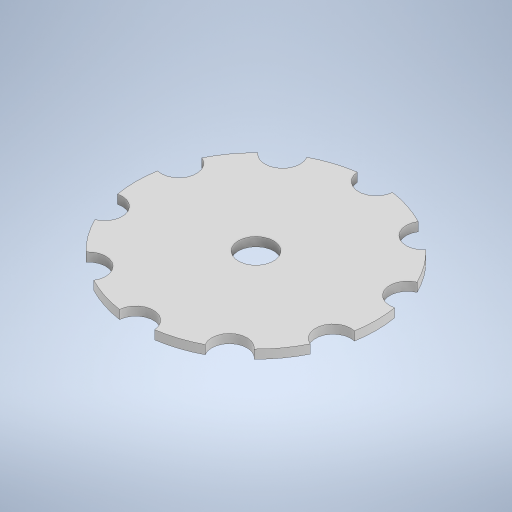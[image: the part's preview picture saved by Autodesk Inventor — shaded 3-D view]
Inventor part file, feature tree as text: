
AUTODESK INVENTOR PART (.ipt)
format: ipt  version: 2024.1 (Build 281209000, 209)  size: 280,576 bytes
history: native  units: mm
features: extrude x1, sketch x1
ambient origin geometry x8: Origin, YZ Plane, XZ Plane, XY Plane, X Axis, Y Axis, Z Axis, Center Point
bodies: Body1 (feature_tree)
feature tree (2):
  extrude  "押し出し2"  Depth=150.0mm
  sketch  "スケッチ1"
